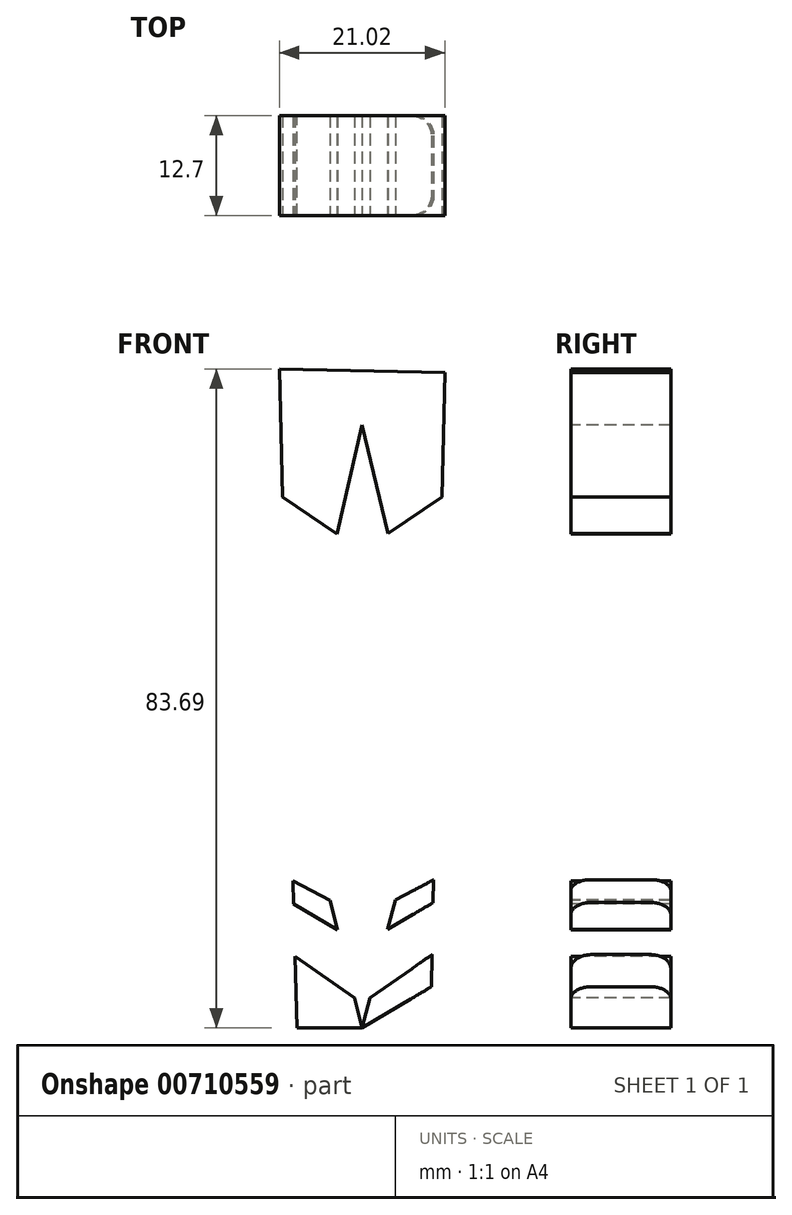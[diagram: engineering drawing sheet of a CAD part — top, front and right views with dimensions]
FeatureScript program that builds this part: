
annotation { "Feature Type Name" : "Feature", "Feature Type Description" : "" }
export const myFeature = defineFeature(function(context is Context, id is Id, definition is map)
    precondition{}
    {
        {
            var Q0;
            Q0=qCreatedBy(makeId("Front.planeOp"),FACE);
            var sketch = newSketch(context, id + "F0", { "sketchPlane" : qUnion([Q0])});
            skLineSegment(sketch, "E0", {"start": v(0, -8.4) * mm, "end": v(-10.52, -8.17) * mm});
            skLineSegment(sketch, "E1", {"start": v(-10.52, -8.17) * mm, "end": v(10.5, -8.63) * mm});
            skLineSegment(sketch, "E2", {"start": v(10.5, -8.63) * mm, "end": v(0, -8.4) * mm});
            skLineSegment(sketch, "E3", {"start": v(-10.52, -8.17) * mm, "end": v(-8.3, -91.86) * mm});
            skLineSegment(sketch, "E4", {"start": v(-8.3, -91.86) * mm, "end": v(-10.52, -8.17) * mm});
            skLineSegment(sketch, "E5", {"start": v(10.5, -8.63) * mm, "end": v(8.67, -91.86) * mm});
            skLineSegment(sketch, "E6", {"start": v(8.67, -91.86) * mm, "end": v(-8.3, -91.86) * mm});
            skSolve(sketch);
        }
        {
            var Q0;
            Q0=makeQuery(id+"F0.imprint","IMPRINT",FACE,{"disambiguationData":[TD([[makeQuery(id+"F0.imprint","IMPRINT",EDGE,{"derivedFrom":sQuery(id+"F0.wireOp",EDGE,"E1")}),-1.0]])]});
            extrude(context, id + "F1", {"entities" : qUnion([Q0]), "depth" : 6.35 * mm, "offsetDistance" : 25.4 * mm});
        }
        {
            var Q0;
            Q0=makeQuery(id+"F1.opExtrude","CAP_FACE",FACE,{"disambiguationData":[OSD([sQuery(id+"F0.wireOp",EDGE,"E1"),sQuery(id+"F0.wireOp",EDGE,"E2"),sQuery(id+"F0.wireOp",EDGE,"E4"),sQuery(id+"F0.wireOp",EDGE,"E5"),sQuery(id+"F0.wireOp",EDGE,"E6")])],"isStart":true});
            extrude(context, id + "F2", {"entities" : qUnion([Q0]), "operationType" : NewBodyOperationType.ADD, "depth" : 6.35 * mm, "offsetDistance" : 25.4 * mm});
        }
        {
            var Q0;
            Q0=makeQuery(id+"F1.opExtrude","CAP_FACE",FACE,{"disambiguationData":[OSD([sQuery(id+"F0.wireOp",EDGE,"E1"),sQuery(id+"F0.wireOp",EDGE,"E2"),sQuery(id+"F0.wireOp",EDGE,"E4"),sQuery(id+"F0.wireOp",EDGE,"E5"),sQuery(id+"F0.wireOp",EDGE,"E6")])],"isStart":false});
            var sketch = newSketch(context, id + "F3", { "sketchPlane" : qUnion([Q0])});
            skLineSegment(sketch, "E7", {"start": v(0, -12.7) * mm, "end": v(-8.4, -8.21) * mm});
            skLineSegment(sketch, "E8", {"start": v(-8.4, -8.21) * mm, "end": v(0, -12.7) * mm});
            skLineSegment(sketch, "E9", {"start": v(0, -15.3) * mm, "end": v(-10.47, -10.2) * mm});
            skLineSegment(sketch, "E10", {"start": v(-10.47, -10.2) * mm, "end": v(0, -15.3) * mm});
            skLineSegment(sketch, "E11", {"start": v(0, -15.3) * mm, "end": v(-9.27, -55.2) * mm});
            skLineSegment(sketch, "E12", {"start": v(-9.27, -55.2) * mm, "end": v(0, -91.86) * mm});
            skLineSegment(sketch, "E13", {"start": v(0, -91.86) * mm, "end": v(9.48, -55.2) * mm});
            skLineSegment(sketch, "E14", {"start": v(9.48, -55.2) * mm, "end": v(0, -15.3) * mm});
            skLineSegment(sketch, "E15", {"start": v(2.66, -26.5) * mm, "end": v(10.21, -21.68) * mm});
            skLineSegment(sketch, "E16", {"start": v(10.21, -21.68) * mm, "end": v(2.66, -26.5) * mm});
            skLineSegment(sketch, "E17", {"start": v(3.27, -29.07) * mm, "end": v(10.15, -24.4) * mm});
            skLineSegment(sketch, "E18", {"start": v(0, -91.86) * mm, "end": v(8.78, -86.64) * mm});
            skLineSegment(sketch, "E19", {"start": v(1, -88.02) * mm, "end": v(8.87, -82.55) * mm});
            skLineSegment(sketch, "E20", {"start": v(4.2, -75.62) * mm, "end": v(9.08, -73.04) * mm});
            skLineSegment(sketch, "E21", {"start": v(3.23, -79.36) * mm, "end": v(9.02, -75.93) * mm});
            skLineSegment(sketch, "E22", {"start": v(0, -44.6) * mm, "end": v(0, -50.7) * mm});
            skLineSegment(sketch, "E23.MirrorCS", {"start": v(-10.21, -21.68) * mm, "end": v(-2.66, -26.5) * mm});
            skLineSegment(sketch, "E24.MirrorCS", {"start": v(-3.27, -29.07) * mm, "end": v(-10.15, -24.4) * mm});
            skLineSegment(sketch, "E25.MirrorCS", {"start": v(10.47, -10.2) * mm, "end": v(0, -15.3) * mm});
            skLineSegment(sketch, "E26.MirrorCS", {"start": v(8.4, -8.21) * mm, "end": v(0, -12.7) * mm});
            skLineSegment(sketch, "E27.MirrorCS", {"start": v(-4.2, -75.62) * mm, "end": v(-9.08, -73.04) * mm});
            skLineSegment(sketch, "E28.MirrorCS", {"start": v(-3.23, -79.36) * mm, "end": v(-9.02, -75.93) * mm});
            skLineSegment(sketch, "E29.MirrorCS", {"start": v(-1, -88.02) * mm, "end": v(-8.87, -82.55) * mm});
            skLineSegment(sketch, "E30.MirrorCS", {"start": v(0, -91.86) * mm, "end": v(-8.78, -86.64) * mm});
            skLineSegment(sketch, "E31", {"start": v(-3.46, -28.94) * mm, "end": v(-3.21, -29.1) * mm});
            skLineSegment(sketch, "E32", {"start": v(-2.67, -26.5) * mm, "end": v(-2.61, -26.53) * mm});
            skLineSegment(sketch, "E33", {"start": v(-4.27, -75.58) * mm, "end": v(-4.1, -75.67) * mm});
            skLineSegment(sketch, "E34", {"start": v(-3.31, -79.31) * mm, "end": v(-3.15, -79.4) * mm});
            skLineSegment(sketch, "E35", {"start": v(-1, -88.01) * mm, "end": v(-0.97, -88.04) * mm});
            skSolve(sketch);
        }
        {
            var Q0;
            {var subQ1=makeQuery(id+"F1.opExtrude","CAP_EDGE",EDGE,{"disambiguationData":[OSD([sQuery(id+"F0.wireOp",EDGE,"E6")])],"isStart":false});var subQ3=makeQuery(id+"F1.opExtrude","CAP_EDGE",EDGE,{"disambiguationData":[OSD([sQuery(id+"F0.wireOp",EDGE,"E4")])],"isStart":false});var subQ5=makeQuery(id+"F3.imprint","INTERSECT",VERTEX,{"derivedFrom":[subQ3,subQ1]});Q0=makeQuery(id+"F3.imprint","IMPRINT",FACE,{"disambiguationData":[TD([[makeQuery(id+"F3.imprint","IMPRINT",EDGE,{"disambiguationData":[TD([[subQ5,-1.0]])],"derivedFrom":subQ3}),-1.0]])]});}
            var Q1;
            {var subQ0=sQuery(id+"F3.wireOp",EDGE,"E18");Q1=makeQuery(id+"F3.imprint","IMPRINT",FACE,{"disambiguationData":[TD([[makeQuery(id+"F3.imprint","IMPRINT",EDGE,{"derivedFrom":subQ0}),-1.0]])]});}
            var Q2;
            {var subQ0=sQuery(id+"F3.wireOp",EDGE,"E19");Q2=makeQuery(id+"F3.imprint","IMPRINT",FACE,{"disambiguationData":[TD([[makeQuery(id+"F3.imprint","IMPRINT",EDGE,{"derivedFrom":subQ0}),1.0]])]});}
            var Q3;
            {var subQ0=sQuery(id+"F3.wireOp",EDGE,"E34");var subQ3=makeQuery(id+"F3.imprint","IMPRINT",VERTEX,{"derivedFrom":subQ0});Q3=makeQuery(id+"F3.imprint","IMPRINT",FACE,{"disambiguationData":[TD([[makeQuery(id+"F3.imprint","IMPRINT",EDGE,{"disambiguationData":[TD([[subQ3,1.0]])],"derivedFrom":subQ0}),-1.0]])]});}
            var Q4;
            {var subQ10=sQuery(id+"F3.wireOp",EDGE,"E11");var subQ13=makeQuery(id+"F3.imprint","INTERSECT",VERTEX,{"derivedFrom":[subQ10,sQuery(id+"F3.wireOp",EDGE,"E31")]});Q4=makeQuery(id+"F3.imprint","IMPRINT",FACE,{"disambiguationData":[TD([[makeQuery(id+"F3.imprint","IMPRINT",EDGE,{"disambiguationData":[TD([[subQ13,1.0]])],"derivedFrom":subQ10}),1.0]])]});}
            var Q5;
            {var subQ0=sQuery(id+"F3.wireOp",EDGE,"E33");var subQ3=makeQuery(id+"F3.imprint","IMPRINT",VERTEX,{"derivedFrom":subQ0});Q5=makeQuery(id+"F3.imprint","IMPRINT",FACE,{"disambiguationData":[TD([[makeQuery(id+"F3.imprint","IMPRINT",EDGE,{"disambiguationData":[TD([[subQ3,1.0]])],"derivedFrom":subQ0}),1.0]])]});}
            var Q6;
            {var subQ3=sQuery(id+"F3.wireOp",EDGE,"E20");Q6=makeQuery(id+"F3.imprint","IMPRINT",FACE,{"disambiguationData":[TD([[makeQuery(id+"F3.imprint","IMPRINT",EDGE,{"derivedFrom":subQ3}),1.0]])]});}
            var Q7;
            {var subQ3=sQuery(id+"F3.wireOp",EDGE,"E17");Q7=makeQuery(id+"F3.imprint","IMPRINT",FACE,{"disambiguationData":[TD([[makeQuery(id+"F3.imprint","IMPRINT",EDGE,{"derivedFrom":subQ3}),-1.0]])]});}
            var Q8;
            {var subQ0=sQuery(id+"F3.wireOp",EDGE,"E31");var subQ3=makeQuery(id+"F3.imprint","IMPRINT",VERTEX,{"derivedFrom":subQ0});Q8=makeQuery(id+"F3.imprint","IMPRINT",FACE,{"disambiguationData":[TD([[makeQuery(id+"F3.imprint","IMPRINT",EDGE,{"disambiguationData":[TD([[subQ3,1.0]])],"derivedFrom":subQ0}),-1.0]])]});}
            var Q9;
            {var subQ8=sQuery(id+"F3.wireOp",EDGE,"E10");Q9=makeQuery(id+"F3.imprint","IMPRINT",FACE,{"disambiguationData":[TD([[makeQuery(id+"F3.imprint","IMPRINT",EDGE,{"derivedFrom":subQ8}),-1.0]])]});}
            var Q10;
            {var subQ3=sQuery(id+"F3.wireOp",EDGE,"E16");Q10=makeQuery(id+"F3.imprint","IMPRINT",FACE,{"disambiguationData":[TD([[makeQuery(id+"F3.imprint","IMPRINT",EDGE,{"derivedFrom":subQ3}),-1.0]])]});}
            var Q11;
            {var subQ0=sQuery(id+"F3.wireOp",EDGE,"E8");Q11=makeQuery(id+"F3.imprint","IMPRINT",FACE,{"disambiguationData":[TD([[makeQuery(id+"F3.imprint","IMPRINT",EDGE,{"derivedFrom":subQ0}),1.0]])]});}
            extrude(context, id + "F4", {"entities" : qUnion([Q0, Q1, Q2, Q3, Q4, Q5, Q6, Q7, Q8, Q9, Q10, Q11]), "operationType" : NewBodyOperationType.REMOVE, "oppositeDirection" : true, "depth" : 25.4 * mm, "offsetDistance" : 25.4 * mm});
        }
        {
            var Q0;
            {var subQ2=sQuery(id+"F0.wireOp",EDGE,"E4");Q0=makeQuery(id+"F4.boolean.opBoolean","SPLIT",EDGE,{"disambiguationData":[TD([makeQuery(id+"F4.opExtrude","SWEPT_FACE",FACE,{"disambiguationData":[OSD([sQuery(id+"F3.wireOp",EDGE,"E10")])]})])],"derivedFrom":makeQuery(id+"F1.opExtrude","CAP_EDGE",EDGE,{"disambiguationData":[OSD([subQ2])],"isStart":false})});}
            var Q1;
            {var subQ0=sQuery(id+"F0.wireOp",EDGE,"E4");Q1=makeQuery(id+"F4.boolean.opBoolean","SPLIT",EDGE,{"disambiguationData":[TD([makeQuery(id+"F4.opExtrude","SWEPT_FACE",FACE,{"disambiguationData":[OSD([sQuery(id+"F3.wireOp",EDGE,"E23.MirrorCS"),sQuery(id+"F3.wireOp",EDGE,"E32")])]})])],"derivedFrom":makeQuery(id+"F1.opExtrude","CAP_EDGE",EDGE,{"disambiguationData":[OSD([subQ0])],"isStart":false})});}
            var Q2;
            {var subQ0=sQuery(id+"F0.wireOp",EDGE,"E4");Q2=makeQuery(id+"F4.boolean.opBoolean","SPLIT",EDGE,{"disambiguationData":[TD([makeQuery(id+"F4.opExtrude","SWEPT_FACE",FACE,{"disambiguationData":[OSD([sQuery(id+"F3.wireOp",EDGE,"E27.MirrorCS"),sQuery(id+"F3.wireOp",EDGE,"E33")])]})])],"derivedFrom":makeQuery(id+"F1.opExtrude","CAP_EDGE",EDGE,{"disambiguationData":[OSD([subQ0])],"isStart":false})});}
            var Q3;
            {var subQ0=sQuery(id+"F0.wireOp",EDGE,"E4");Q3=makeQuery(id+"F4.boolean.opBoolean","SPLIT",EDGE,{"disambiguationData":[TD([makeQuery(id+"F4.opExtrude","SWEPT_FACE",FACE,{"disambiguationData":[OSD([sQuery(id+"F3.wireOp",EDGE,"E30.MirrorCS")])]})])],"derivedFrom":makeQuery(id+"F1.opExtrude","CAP_EDGE",EDGE,{"disambiguationData":[OSD([subQ0])],"isStart":false})});}
            var Q4;
            {var subQ0=sQuery(id+"F0.wireOp",EDGE,"E4");Q4=makeQuery(id+"F4.boolean.opBoolean","SPLIT",EDGE,{"disambiguationData":[TD([makeQuery(id+"F4.opExtrude","SWEPT_FACE",FACE,{"disambiguationData":[OSD([sQuery(id+"F3.wireOp",EDGE,"E27.MirrorCS"),sQuery(id+"F3.wireOp",EDGE,"E33")])]})])],"derivedFrom":makeQuery(id+"F2.opExtrude","CAP_EDGE",EDGE,{"disambiguationData":[OSD([subQ0])],"isStart":false})});}
            var Q5;
            {var subQ0=sQuery(id+"F0.wireOp",EDGE,"E4");Q5=makeQuery(id+"F4.boolean.opBoolean","SPLIT",EDGE,{"disambiguationData":[TD([makeQuery(id+"F4.opExtrude","SWEPT_FACE",FACE,{"disambiguationData":[OSD([sQuery(id+"F3.wireOp",EDGE,"E30.MirrorCS")])]})])],"derivedFrom":makeQuery(id+"F2.opExtrude","CAP_EDGE",EDGE,{"disambiguationData":[OSD([subQ0])],"isStart":false})});}
            var Q6;
            {var subQ0=sQuery(id+"F0.wireOp",EDGE,"E5");Q6=makeQuery(id+"F4.boolean.opBoolean","SPLIT",EDGE,{"disambiguationData":[TD([makeQuery(id+"F4.opExtrude","SWEPT_FACE",FACE,{"disambiguationData":[OSD([sQuery(id+"F3.wireOp",EDGE,"E20")])]})])],"derivedFrom":makeQuery(id+"F1.opExtrude","CAP_EDGE",EDGE,{"disambiguationData":[OSD([subQ0])],"isStart":false})});}
            var Q7;
            {var subQ0=sQuery(id+"F0.wireOp",EDGE,"E5");Q7=makeQuery(id+"F4.boolean.opBoolean","SPLIT",EDGE,{"disambiguationData":[TD([makeQuery(id+"F4.opExtrude","SWEPT_FACE",FACE,{"disambiguationData":[OSD([sQuery(id+"F3.wireOp",EDGE,"E18")])]})])],"derivedFrom":makeQuery(id+"F1.opExtrude","CAP_EDGE",EDGE,{"disambiguationData":[OSD([subQ0])],"isStart":false})});}
            var Q8;
            {var subQ0=sQuery(id+"F0.wireOp",EDGE,"E4");Q8=makeQuery(id+"F4.boolean.opBoolean","SPLIT",EDGE,{"disambiguationData":[TD([makeQuery(id+"F4.opExtrude","SWEPT_FACE",FACE,{"disambiguationData":[OSD([sQuery(id+"F3.wireOp",EDGE,"E10")])]})])],"derivedFrom":makeQuery(id+"F2.opExtrude","CAP_EDGE",EDGE,{"disambiguationData":[OSD([subQ0])],"isStart":false})});}
            var Q9;
            {var subQ0=sQuery(id+"F0.wireOp",EDGE,"E4");Q9=makeQuery(id+"F4.boolean.opBoolean","SPLIT",EDGE,{"disambiguationData":[TD([makeQuery(id+"F4.opExtrude","SWEPT_FACE",FACE,{"disambiguationData":[OSD([sQuery(id+"F3.wireOp",EDGE,"E23.MirrorCS"),sQuery(id+"F3.wireOp",EDGE,"E32")])]})])],"derivedFrom":makeQuery(id+"F2.opExtrude","CAP_EDGE",EDGE,{"disambiguationData":[OSD([subQ0])],"isStart":false})});}
            var Q10;
            {var subQ0=sQuery(id+"F0.wireOp",EDGE,"E5");Q10=makeQuery(id+"F4.boolean.opBoolean","SPLIT",EDGE,{"disambiguationData":[TD([makeQuery(id+"F4.opExtrude","SWEPT_FACE",FACE,{"disambiguationData":[OSD([sQuery(id+"F3.wireOp",EDGE,"E16")])]})])],"derivedFrom":makeQuery(id+"F1.opExtrude","CAP_EDGE",EDGE,{"disambiguationData":[OSD([subQ0])],"isStart":false})});}
            var Q11;
            {var subQ2=sQuery(id+"F0.wireOp",EDGE,"E5");Q11=makeQuery(id+"F4.boolean.opBoolean","SPLIT",EDGE,{"disambiguationData":[TD([makeQuery(id+"F4.opExtrude","SWEPT_FACE",FACE,{"disambiguationData":[OSD([sQuery(id+"F3.wireOp",EDGE,"E25.MirrorCS")])]})])],"derivedFrom":makeQuery(id+"F1.opExtrude","CAP_EDGE",EDGE,{"disambiguationData":[OSD([subQ2])],"isStart":false})});}
            var Q12;
            {var subQ0=sQuery(id+"F0.wireOp",EDGE,"E5");Q12=makeQuery(id+"F4.boolean.opBoolean","SPLIT",EDGE,{"disambiguationData":[TD([makeQuery(id+"F4.opExtrude","SWEPT_FACE",FACE,{"disambiguationData":[OSD([sQuery(id+"F3.wireOp",EDGE,"E25.MirrorCS")])]})])],"derivedFrom":makeQuery(id+"F2.opExtrude","CAP_EDGE",EDGE,{"disambiguationData":[OSD([subQ0])],"isStart":false})});}
            var Q13;
            {var subQ0=sQuery(id+"F0.wireOp",EDGE,"E5");Q13=makeQuery(id+"F4.boolean.opBoolean","SPLIT",EDGE,{"disambiguationData":[TD([makeQuery(id+"F4.opExtrude","SWEPT_FACE",FACE,{"disambiguationData":[OSD([sQuery(id+"F3.wireOp",EDGE,"E16")])]})])],"derivedFrom":makeQuery(id+"F2.opExtrude","CAP_EDGE",EDGE,{"disambiguationData":[OSD([subQ0])],"isStart":false})});}
            var Q14;
            {var subQ0=sQuery(id+"F0.wireOp",EDGE,"E5");Q14=makeQuery(id+"F4.boolean.opBoolean","SPLIT",EDGE,{"disambiguationData":[TD([makeQuery(id+"F4.opExtrude","SWEPT_FACE",FACE,{"disambiguationData":[OSD([sQuery(id+"F3.wireOp",EDGE,"E18")])]})])],"derivedFrom":makeQuery(id+"F2.opExtrude","CAP_EDGE",EDGE,{"disambiguationData":[OSD([subQ0])],"isStart":false})});}
            var Q15;
            {var subQ0=sQuery(id+"F0.wireOp",EDGE,"E5");Q15=makeQuery(id+"F4.boolean.opBoolean","SPLIT",EDGE,{"disambiguationData":[TD([makeQuery(id+"F4.opExtrude","SWEPT_FACE",FACE,{"disambiguationData":[OSD([sQuery(id+"F3.wireOp",EDGE,"E20")])]})])],"derivedFrom":makeQuery(id+"F2.opExtrude","CAP_EDGE",EDGE,{"disambiguationData":[OSD([subQ0])],"isStart":false})});}
            fillet(context, id + "F5", {"entities" : qUnion([Q0, Q1, Q2, Q3, Q4, Q5, Q6, Q7, Q8, Q9, Q10, Q11, Q12, Q13, Q14, Q15]), "radius" : 2.54 * mm, "tangentPropagation" : true, "allowEdgeOverflow" : false});
        }
    });
